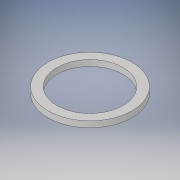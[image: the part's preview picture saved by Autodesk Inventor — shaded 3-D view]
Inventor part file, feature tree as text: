
AUTODESK INVENTOR PART (.ipt)
format: ipt  version: 2018 (Build 220112000, 112)  size: 99,328 bytes
history: native  units: in
note: dims shown in document units (in); Inventor stores cm internally (conversion verified against a paired STEP export)
features: extrude x1, sketch x1
ambient origin geometry x8: Origin, YZ Plane, XZ Plane, XY Plane, X Axis, Y Axis, Z Axis, Center Point
bodies: Solid1 (feature_tree)
feature tree (2):
  extrude  "Extrusion1"  Depth=0.05in
  sketch  "Sketch1"  dims[d0=0.55in d1=0.7in d2=0.05in d3=0.0in]
